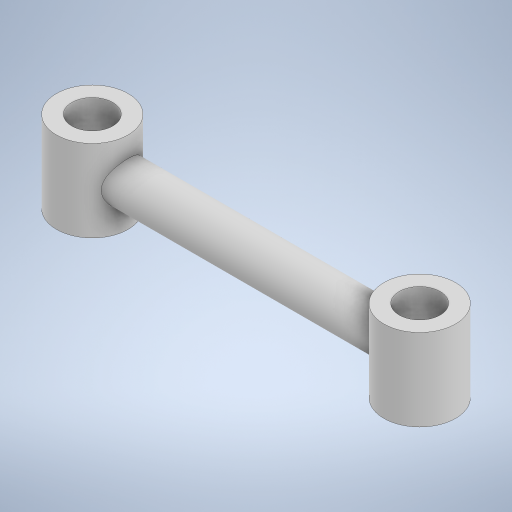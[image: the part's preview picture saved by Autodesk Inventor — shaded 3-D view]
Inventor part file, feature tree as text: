
AUTODESK INVENTOR PART (.ipt)
format: ipt  version: 2024 (Build 280153000, 153)  size: 260,608 bytes
history: native  units: in
note: dims shown in document units (in); Inventor stores cm internally (conversion verified against a paired STEP export)
features: sketch x3, extrude x3, revolve x1, mirror x1
ambient origin geometry x8: Origin, YZ Plane, XZ Plane, XY Plane, X Axis, Y Axis, Z Axis, Center Point
bodies: Solid1 (feature_tree)
feature tree (8):
  revolve  "Revolution1"  [1 undecoded]
  sketch  "Sketch2"  dims[d2=90.0deg d3=0.7874in]
  extrude  "Extrusion1"  Depth=0.7874in
  extrude  "Extrusion2"  Depth=1.5748in TaperAngle=0.0deg
  mirror  "Mirror1"
  extrude  "Extrusion3"  Depth=1.5748in TaperAngle=0.0deg
  sketch  "Sketch1"  dims[d0=6.2992in d1=0.3937in]
  sketch  "Sketch3"  dims[d4=1.378in d5=1.5748in d6=0.0in d7=1.5748in d8=0.0in d9=0.7874in d10=1.5748in d11=0.0in]
note: 1 required parameter value undecoded (feature->parameter linkage not recoverable at this tier; creation-order binding heuristic only, values carry confidence <= 0.55)
